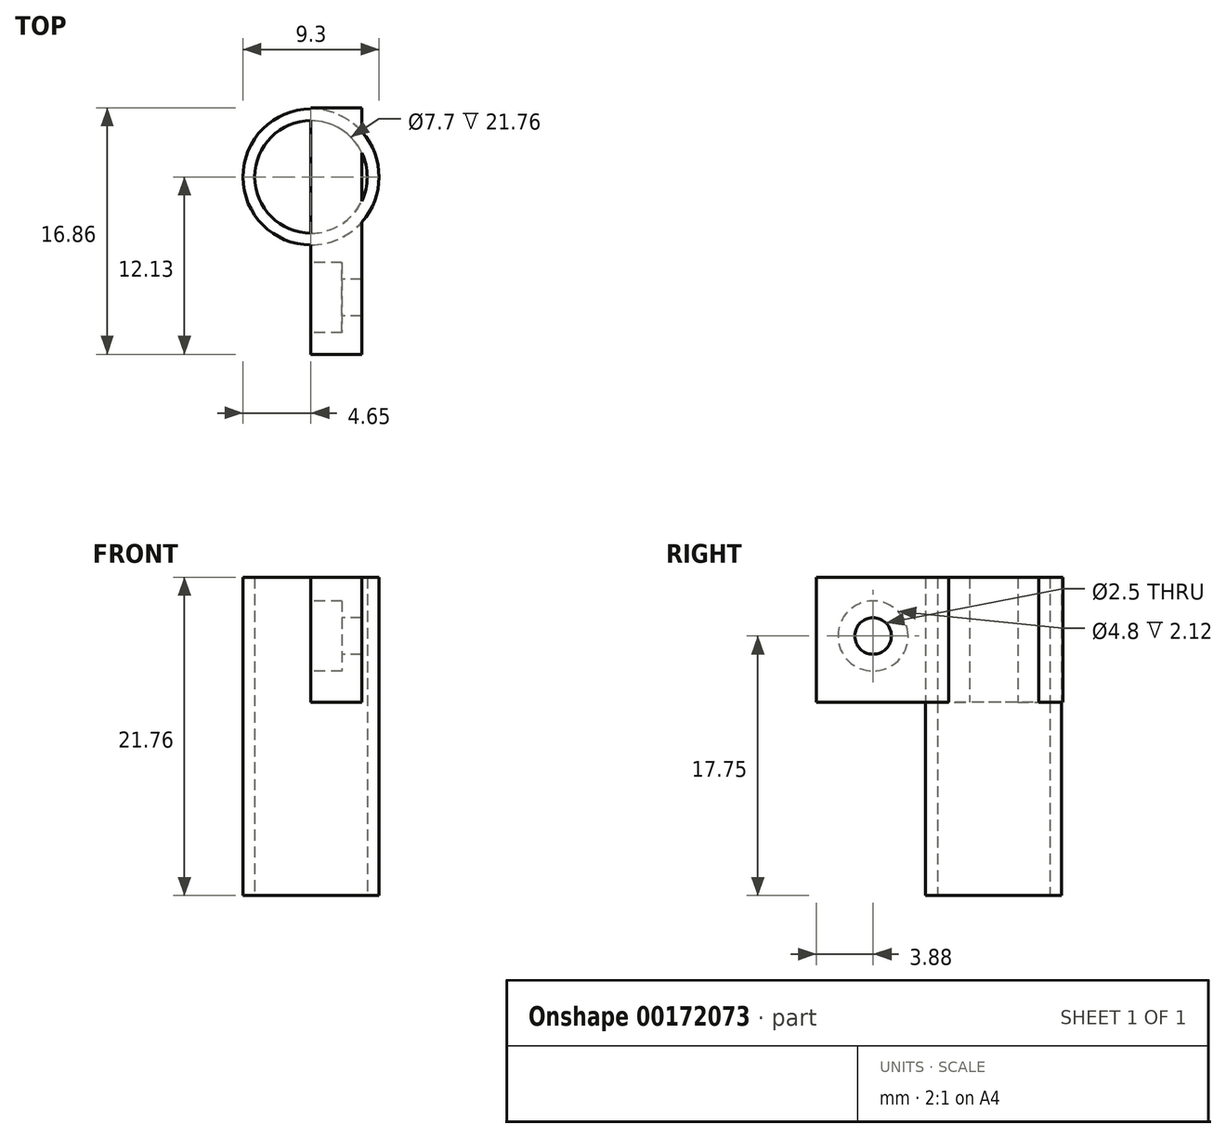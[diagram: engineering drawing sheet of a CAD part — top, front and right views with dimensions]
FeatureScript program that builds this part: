
annotation { "Feature Type Name" : "Feature", "Feature Type Description" : "" }
export const myFeature = defineFeature(function(context is Context, id is Id, definition is map)
    precondition{}
    {
        {
            var Q0;
            Q0=qCreatedBy(makeId("Top.planeOp"),FACE);
            var sketch = newSketch(context, id + "F0", { "sketchPlane" : qUnion([Q0])});
            skCircle(sketch, "E0", {"center": v(0, 0) * mm, "radius": 4.65 * mm});
            skCircle(sketch, "E1", {"center": v(0, 0) * mm, "radius": 3.85 * mm});
            skSolve(sketch);
        }
        {
            var Q0;
            Q0=makeQuery(id+"F0.imprint","IMPRINT",FACE,{"disambiguationData":[TD([[makeQuery(id+"F0.imprint","IMPRINT",EDGE,{"derivedFrom":sQuery(id+"F0.wireOp",EDGE,"E0")}),1.0]])]});
            extrude(context, id + "F1", {"entities" : qUnion([Q0]), "depth" : 8.53 * mm});
        }
        {
            var Q0;
            Q0=qCreatedBy(makeId("Right.planeOp"),FACE);
            var sketch = newSketch(context, id + "F2", { "sketchPlane" : qUnion([Q0])});
            skLineSegment(sketch, "E2.bottom", {"start": v(4.73, 8.53) * mm, "end": v(-12.13, 8.53) * mm});
            skLineSegment(sketch, "E2.top", {"start": v(4.73, 0) * mm, "end": v(-12.13, 0) * mm});
            skLineSegment(sketch, "E2.left", {"start": v(4.73, 8.53) * mm, "end": v(4.73, 0) * mm});
            skLineSegment(sketch, "E2.right", {"start": v(-12.13, 8.53) * mm, "end": v(-12.13, 0) * mm});
            skSolve(sketch);
        }
        {
            var Q0;
            Q0=makeQuery(id+"F2.imprint","IMPRINT",FACE,{"disambiguationData":[TD([[makeQuery(id+"F2.imprint","IMPRINT",EDGE,{"derivedFrom":sQuery(id+"F2.wireOp",EDGE,"E2.bottom")}),1.0]])]});
            extrude(context, id + "F3", {"entities" : qUnion([Q0]), "operationType" : NewBodyOperationType.ADD, "depth" : 3.48 * mm});
        }
        {
            var Q0;
            {var subQ0=sQuery(id+"F2.wireOp",EDGE,"E2.top");var subQ1=sQuery(id+"F2.wireOp",EDGE,"E2.bottom");var subQ3=sQuery(id+"F2.wireOp",EDGE,"E2.right");Q0=makeQuery(id+"F3.boolean.opBoolean","SPLIT",FACE,{"disambiguationData":[TD([makeQuery(id+"F3.opExtrude","SWEPT_FACE",FACE,{"disambiguationData":[OSD([subQ3])]})])],"derivedFrom":makeQuery(id+"F3.opExtrude","CAP_FACE",FACE,{"disambiguationData":[OSD([subQ1,subQ0,sQuery(id+"F2.wireOp",EDGE,"E2.left"),subQ3])],"isStart":true})});}
            var sketch = newSketch(context, id + "F4", { "sketchPlane" : qUnion([Q0])});
            skCircle(sketch, "E3", {"center": v(8.25, 4.52) * mm, "radius": 1.25 * mm});
            skPoint(sketch, "E4.centerSnap0", {"position": v(4.65, 4.26) * mm});
            skCircle(sketch, "E5", {"center": v(8.25, 4.52) * mm, "radius": 2.4 * mm});
            skSolve(sketch);
        }
        {
            var Q0;
            Q0=makeQuery(id+"F4.imprint","IMPRINT",FACE,{"disambiguationData":[TD([[makeQuery(id+"F4.imprint","IMPRINT",EDGE,{"derivedFrom":sQuery(id+"F4.wireOp",EDGE,"E3")}),1.0]])]});
            extrude(context, id + "F5", {"entities" : qUnion([Q0]), "operationType" : NewBodyOperationType.REMOVE, "oppositeDirection" : true, "depth" : 25 * mm});
        }
        {
            var Q0;
            Q0 = qSketchRegion(id + "F4", true);
            extrude(context, id + "F6", {"entities" : qUnion([Q0]), "operationType" : NewBodyOperationType.REMOVE, "oppositeDirection" : true, "depth" : 2.12 * mm});
        }
        {
            var Q0;
            Q0 = qSketchRegion(id + "F0", true);
            extrude(context, id + "F7", {"entities" : qUnion([Q0]), "operationType" : NewBodyOperationType.ADD, "oppositeDirection" : true, "depth" : 13.23 * mm});
        }
    });
